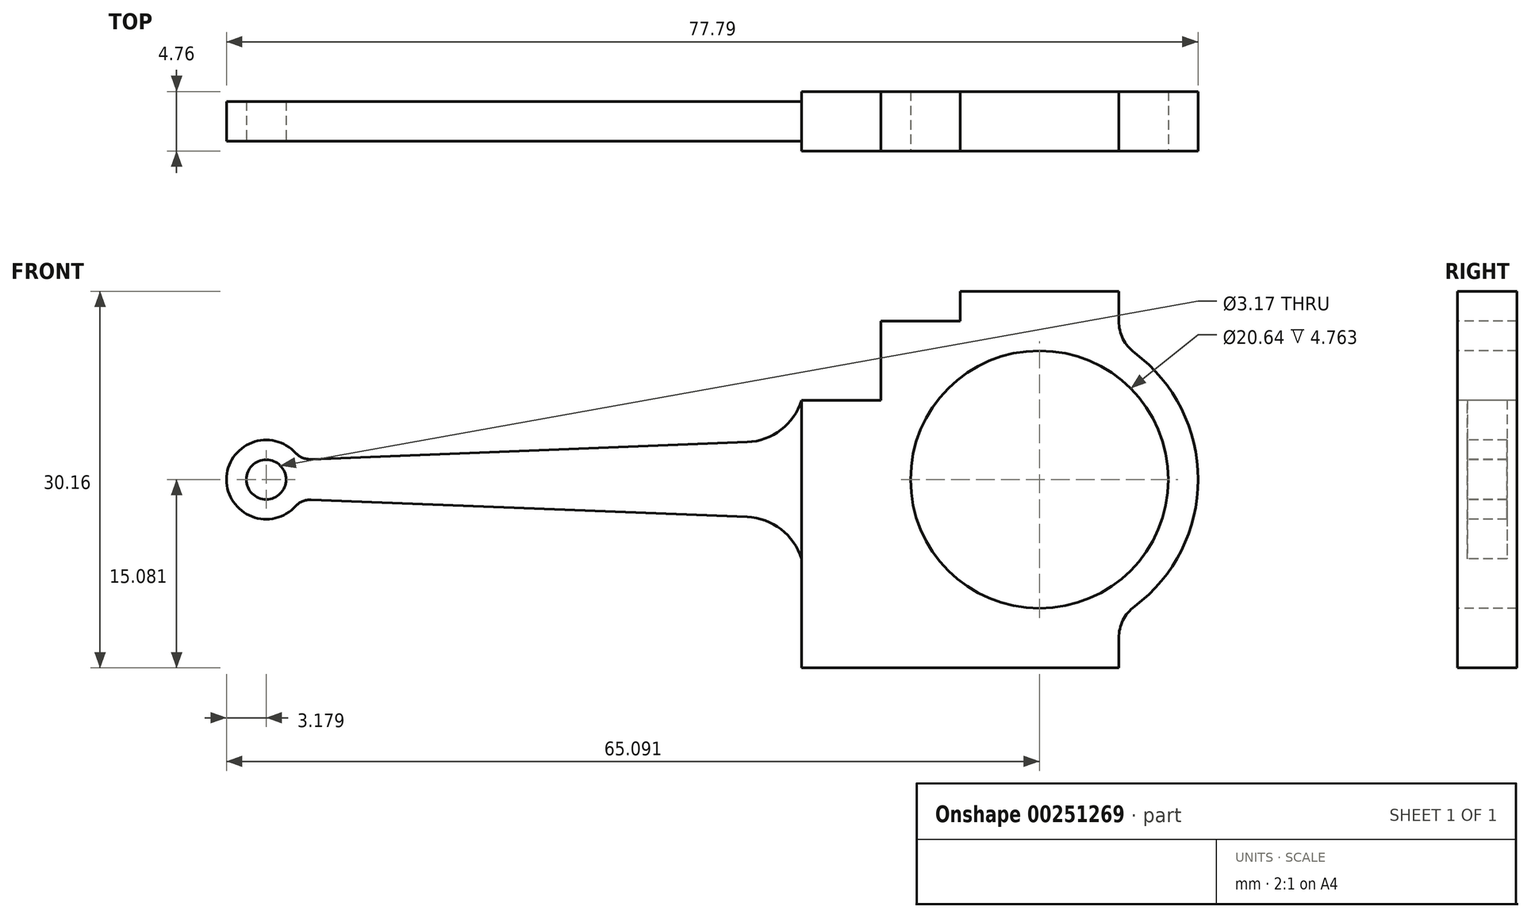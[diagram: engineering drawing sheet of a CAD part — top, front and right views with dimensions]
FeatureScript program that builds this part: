
annotation { "Feature Type Name" : "Feature", "Feature Type Description" : "" }
export const myFeature = defineFeature(function(context is Context, id is Id, definition is map)
    precondition{}
    {
        {
            var Q0;
            Q0=qCreatedBy(makeId("Top.planeOp"),FACE);
            var sketch = newSketch(context, id + "F0", { "sketchPlane" : qUnion([Q0])});
            skLineSegment(sketch, "E0", {"start": v(-28.4, 19.75) * mm, "end": v(17.64, 19.75) * mm});
            skLineSegment(sketch, "E1", {"start": v(17.64, 19.75) * mm, "end": v(17.64, 20.54) * mm});
            skLineSegment(sketch, "E2", {"start": v(17.64, 20.54) * mm, "end": v(49.4, 20.54) * mm});
            skLineSegment(sketch, "E3", {"start": v(49.4, 20.54) * mm, "end": v(49.4, 15.78) * mm});
            skLineSegment(sketch, "E4", {"start": v(49.4, 15.78) * mm, "end": v(17.64, 15.78) * mm});
            skLineSegment(sketch, "E5", {"start": v(17.64, 15.78) * mm, "end": v(17.64, 16.57) * mm});
            skLineSegment(sketch, "E6", {"start": v(17.64, 16.57) * mm, "end": v(-28.4, 16.57) * mm});
            skLineSegment(sketch, "E7", {"start": v(-28.4, 16.57) * mm, "end": v(-28.4, 19.75) * mm});
            skSolve(sketch);
        }
        {
            var Q0;
            Q0 = qSketchRegion(id + "F0", true);
            extrude(context, id + "F1", {"entities" : qUnion([Q0]), "depth" : 30.16 * mm});
        }
        {
            var Q0;
            Q0=makeQuery(id+"F1.opExtrude","SWEPT_FACE",FACE,{"disambiguationData":[OSD([sQuery(id+"F0.wireOp",EDGE,"E6")])]});
            var sketch = newSketch(context, id + "F2", { "sketchPlane" : qUnion([Q0])});
            skCircle(sketch, "E8", {"center": v(-25.22, 15.08) * mm, "radius": 1.59 * mm});
            skCircle(sketch, "E9", {"center": v(-25.22, 15.08) * mm, "radius": 3.18 * mm});
            skLineSegment(sketch, "E10", {"start": v(-25.22, 15.08) * mm, "end": v(17.64, 15.08) * mm, "construction": true});
            skLineSegment(sketch, "E11", {"start": v(-22.47, 16.67) * mm, "end": v(17.64, 18.26) * mm});
            skLineSegment(sketch, "E12", {"start": v(-22.47, 13.5) * mm, "end": v(17.64, 11.9) * mm});
            skArc(sketch, "E13", {"start": v(-22.87, 17.22) * mm, "mid": v(-22.31, 16.82) * mm, "end": v(-21.64, 16.7) * mm});
            skArc(sketch, "E14", {"start": v(-21.64, 13.46) * mm, "mid": v(-22.31, 13.34) * mm, "end": v(-22.87, 12.94) * mm});
            skArc(sketch, "E15", {"start": v(13.28, 18.08) * mm, "mid": v(16, 19.06) * mm, "end": v(17.64, 21.43) * mm});
            skArc(sketch, "E16", {"start": v(17.64, 8.73) * mm, "mid": v(16, 11.1) * mm, "end": v(13.28, 12.08) * mm});
            skSolve(sketch);
        }
        {
            var Q0;
            Q0=makeQuery(id+"F2.imprint","IMPRINT",FACE,{"disambiguationData":[TD([[makeQuery(id+"F2.imprint","IMPRINT",EDGE,{"derivedFrom":sQuery(id+"F2.wireOp",EDGE,"E8")}),1.0]])]});
            var Q1;
            {var subQ1=sQuery(id+"F2.wireOp",EDGE,"E13");Q1=makeQuery(id+"F2.imprint","IMPRINT",FACE,{"disambiguationData":[TD([[makeQuery(id+"F2.imprint","IMPRINT",EDGE,{"derivedFrom":subQ1}),1.0]])]});}
            var Q2;
            {var subQ1=sQuery(id+"F2.wireOp",EDGE,"E14");Q2=makeQuery(id+"F2.imprint","IMPRINT",FACE,{"disambiguationData":[TD([[makeQuery(id+"F2.imprint","IMPRINT",EDGE,{"derivedFrom":subQ1}),1.0]])]});}
            extrude(context, id + "F3", {"entities" : qUnion([Q0, Q1, Q2]), "operationType" : NewBodyOperationType.REMOVE, "oppositeDirection" : true, "depth" : 25.4 * mm});
        }
        {
            var Q0;
            Q0=makeQuery(id+"F1.opExtrude","SWEPT_FACE",FACE,{"disambiguationData":[OSD([sQuery(id+"F0.wireOp",EDGE,"E4")])]});
            var sketch = newSketch(context, id + "F4", { "sketchPlane" : qUnion([Q0])});
            skCircle(sketch, "E17", {"center": v(36.7, 15.08) * mm, "radius": 10.32 * mm});
            skCircle(sketch, "E18.0", {"center": v(-25.22, 15.08) * mm, "radius": 1.59 * mm});
            skCircle(sketch, "E19", {"center": v(36.7, 15.08) * mm, "radius": 12.7 * mm});
            skArc(sketch, "E20.0", {"start": v(13.28, 18.08) * mm, "mid": v(16, 19.06) * mm, "end": v(17.64, 21.43) * mm});
            skArc(sketch, "E21.0", {"start": v(17.64, 8.73) * mm, "mid": v(16, 11.1) * mm, "end": v(13.28, 12.08) * mm});
            skLineSegment(sketch, "E22", {"start": v(17.64, 8.73) * mm, "end": v(25.7, 8.73) * mm});
            skLineSegment(sketch, "E23", {"start": v(17.64, 21.43) * mm, "end": v(24, 21.43) * mm});
            skLineSegment(sketch, "E24", {"start": v(24, 21.43) * mm, "end": v(24, 27.78) * mm});
            skLineSegment(sketch, "E25", {"start": v(24, 27.78) * mm, "end": v(30.34, 27.78) * mm});
            skLineSegment(sketch, "E26", {"start": v(30.34, 27.78) * mm, "end": v(30.34, 30.16) * mm});
            skLineSegment(sketch, "E27", {"start": v(30.34, 0) * mm, "end": v(30.34, 4.08) * mm});
            skLineSegment(sketch, "E28", {"start": v(43.04, 30.16) * mm, "end": v(43.04, 26.08) * mm});
            skLineSegment(sketch, "E29", {"start": v(43.04, 0) * mm, "end": v(43.04, 4.08) * mm});
            skArc(sketch, "E30", {"start": v(43.04, 27.78) * mm, "mid": v(43.38, 26.36) * mm, "end": v(44.31, 25.24) * mm});
            skArc(sketch, "E31", {"start": v(26.53, 7.46) * mm, "mid": v(25.41, 8.4) * mm, "end": v(24, 8.73) * mm});
            skArc(sketch, "E32", {"start": v(30.34, 2.38) * mm, "mid": v(30, 3.8) * mm, "end": v(29.07, 4.92) * mm});
            skArc(sketch, "E33", {"start": v(44.31, 4.92) * mm, "mid": v(43.38, 3.8) * mm, "end": v(43.04, 2.38) * mm});
            skSolve(sketch);
        }
        {
            var Q0;
            Q0=makeQuery(id+"F4.imprint","IMPRINT",FACE,{"disambiguationData":[TD([[makeQuery(id+"F4.imprint","IMPRINT",EDGE,{"derivedFrom":sQuery(id+"F4.wireOp",EDGE,"E18.0")}),1.0]])]});
            var Q1;
            {var subQ8=sQuery(id+"F4.wireOp",EDGE,"E30");Q1=makeQuery(id+"F4.imprint","IMPRINT",FACE,{"disambiguationData":[TD([[makeQuery(id+"F4.imprint","IMPRINT",EDGE,{"derivedFrom":subQ8}),1.0]])]});}
            var Q2;
            {var subQ5=sQuery(id+"F4.wireOp",EDGE,"E23");Q2=makeQuery(id+"F4.imprint","IMPRINT",FACE,{"disambiguationData":[TD([[makeQuery(id+"F4.imprint","IMPRINT",EDGE,{"derivedFrom":subQ5}),1.0]])]});}
            var Q3;
            {var subQ8=sQuery(id+"F4.wireOp",EDGE,"E33");Q3=makeQuery(id+"F4.imprint","IMPRINT",FACE,{"disambiguationData":[TD([[makeQuery(id+"F4.imprint","IMPRINT",EDGE,{"derivedFrom":subQ8}),1.0]])]});}
            var Q4;
            {var subQ0=sQuery(id+"F4.wireOp",EDGE,"E31");Q4=makeQuery(id+"F4.imprint","IMPRINT",FACE,{"disambiguationData":[TD([[makeQuery(id+"F4.imprint","IMPRINT",EDGE,{"derivedFrom":subQ0}),1.0]])]});}
            var Q5;
            Q5=makeQuery(id+"F4.imprint","IMPRINT",FACE,{"disambiguationData":[TD([[makeQuery(id+"F4.imprint","IMPRINT",EDGE,{"derivedFrom":sQuery(id+"F4.wireOp",EDGE,"E17")}),1.0]])]});
            extrude(context, id + "F5", {"entities" : qUnion([Q0, Q1, Q2, Q3, Q4, Q5]), "operationType" : NewBodyOperationType.REMOVE, "oppositeDirection" : true, "depth" : 25.4 * mm});
        }
    });
